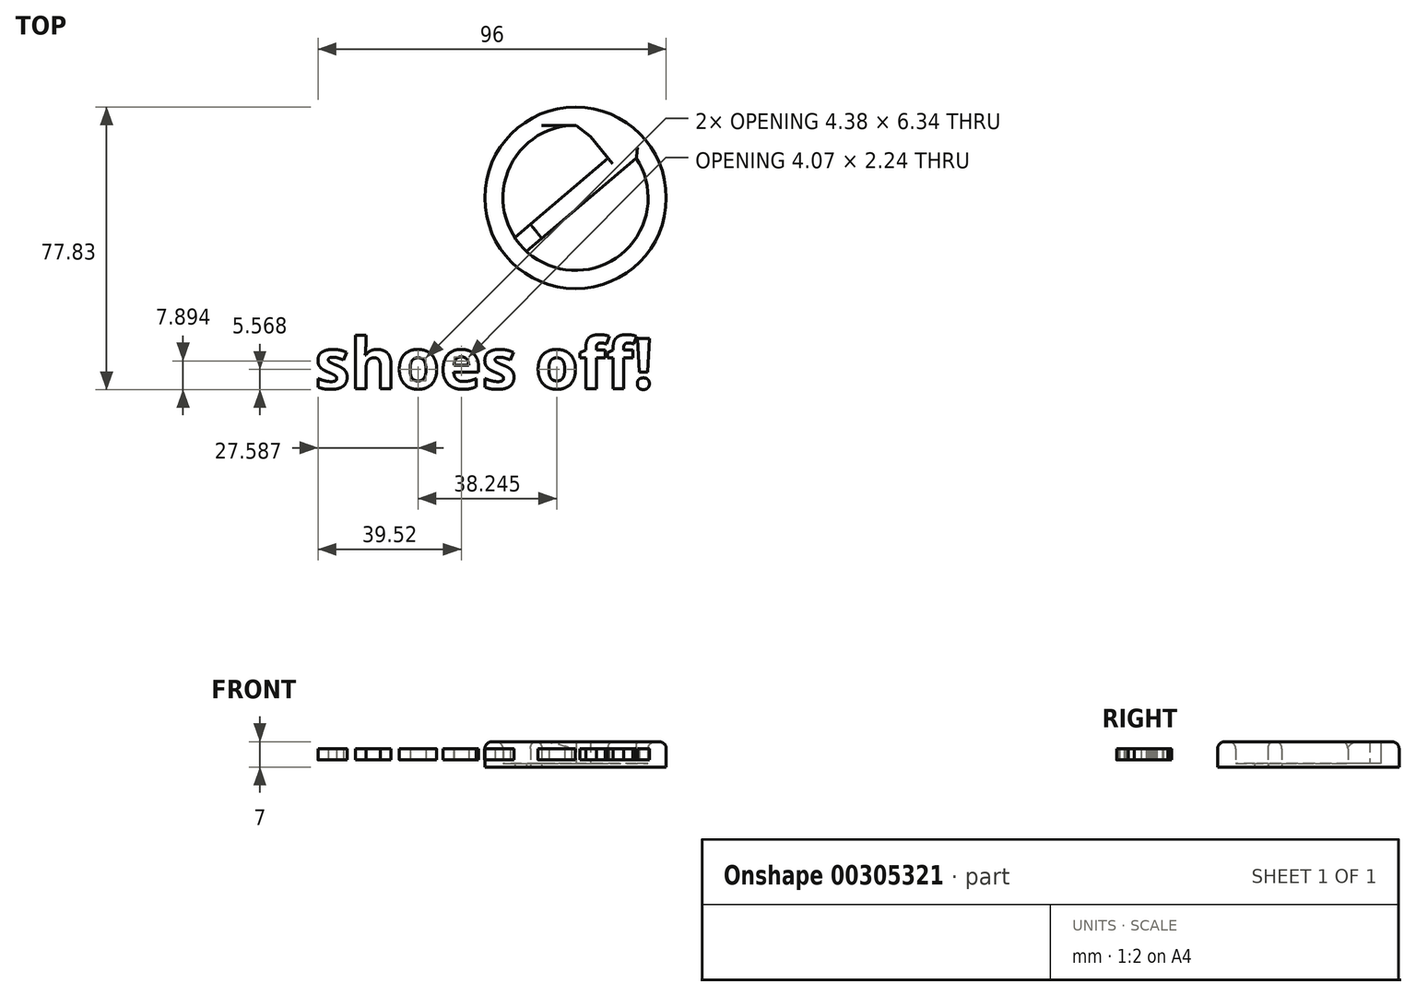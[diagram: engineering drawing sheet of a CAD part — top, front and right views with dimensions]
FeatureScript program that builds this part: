
annotation { "Feature Type Name" : "Feature", "Feature Type Description" : "" }
export const myFeature = defineFeature(function(context is Context, id is Id, definition is map)
    precondition{}
    {
        {
            var Q0;
            Q0=qCreatedBy(makeId("Top.planeOp"),FACE);
            var sketch = newSketch(context, id + "F0", { "sketchPlane" : qUnion([Q0])});
            skLineSegment(sketch, "E0.top", {"start": v(-121.35, -25.22) * mm, "end": v(78.65, -25.22) * mm});
            skLineSegment(sketch, "E0.left", {"start": v(-121.35, 24.78) * mm, "end": v(-121.35, -25.22) * mm});
            skLineSegment(sketch, "E0.right", {"start": v(78.65, 24.78) * mm, "end": v(78.65, -25.22) * mm});
            skCircle(sketch, "E1", {"center": v(37.04, 37.35) * mm, "radius": 25 * mm});
            skPoint(sketch, "E1.first.point", {"position": v(15.44, 24.78) * mm});
            skCircle(sketch, "E2", {"center": v(37.04, 37.35) * mm, "radius": 20 * mm});
            skLineSegment(sketch, "E3", {"start": v(20.32, 26.39) * mm, "end": v(50.53, 52.12) * mm});
            skLineSegment(sketch, "E4", {"start": v(53.77, 48.31) * mm, "end": v(23.56, 22.58) * mm});
            skLineSegment(sketch, "E5", {"start": v(20.32, 26.39) * mm, "end": v(23.56, 22.58) * mm, "construction": true});
            skLineSegment(sketch, "E6", {"start": v(21.94, 24.48) * mm, "end": v(52.27, 50.32) * mm, "construction": true});
            skPoint(sketch, "E7", {"position": v(58.65, 24.78) * mm});
            skLineSegment(sketch, "E8", {"start": v(-121.35, 24.78) * mm, "end": v(15.44, 24.78) * mm});
            skLineSegment(sketch, "E9", {"start": v(58.65, 24.78) * mm, "end": v(78.65, 24.78) * mm});
            skLineSegment(sketch, "E10", {"start": v(30.68, 24.1) * mm, "end": v(36.58, 27.82) * mm});
            skLineSegment(sketch, "E11", {"start": v(36.58, 27.82) * mm, "end": v(35.77, 32.31) * mm});
            skLineSegment(sketch, "E12", {"start": v(34.65, 36) * mm, "end": v(32.57, 40.8) * mm});
            skLineSegment(sketch, "E13", {"start": v(32.57, 40.8) * mm, "end": v(29.04, 43.21) * mm});
            skLineSegment(sketch, "E14", {"start": v(29.04, 43.21) * mm, "end": v(24.28, 43.73) * mm});
            skLineSegment(sketch, "E15", {"start": v(24.28, 43.73) * mm, "end": v(21.68, 41.4) * mm});
            skLineSegment(sketch, "E16", {"start": v(21.68, 41.4) * mm, "end": v(20.64, 36.9) * mm});
            skLineSegment(sketch, "E17", {"start": v(20.64, 36.9) * mm, "end": v(22.8, 32.31) * mm});
            skLineSegment(sketch, "E18", {"start": v(22.8, 32.31) * mm, "end": v(27.74, 26.17) * mm});
            skLineSegment(sketch, "E19", {"start": v(27.74, 26.17) * mm, "end": v(30.68, 24.1) * mm});
            skLineSegment(sketch, "E20", {"start": v(31.8, 22.28) * mm, "end": v(37.95, 26.17) * mm});
            skLineSegment(sketch, "E21", {"start": v(37.95, 26.17) * mm, "end": v(39.94, 24.61) * mm});
            skLineSegment(sketch, "E22", {"start": v(39.94, 24.61) * mm, "end": v(41.5, 22.02) * mm});
            skLineSegment(sketch, "E23", {"start": v(41.5, 22.02) * mm, "end": v(40.72, 18.47) * mm});
            skLineSegment(sketch, "E24", {"start": v(40.72, 18.47) * mm, "end": v(38.2, 17.09) * mm});
            skLineSegment(sketch, "E25", {"start": v(38.2, 17.09) * mm, "end": v(34.23, 17.78) * mm});
            skLineSegment(sketch, "E26", {"start": v(34.23, 17.78) * mm, "end": v(32.76, 20.03) * mm});
            skLineSegment(sketch, "E27", {"start": v(32.76, 20.03) * mm, "end": v(31.8, 22.28) * mm});
            skLineSegment(sketch, "E28", {"start": v(34.65, 36) * mm, "end": v(35.77, 32.31) * mm});
            skLineSegment(sketch, "E29", {"start": v(25.33, 53.56) * mm, "end": v(50.32, 22.39) * mm, "construction": true});
            skLineSegment(sketch, "E30.MirrorCS", {"start": v(29.21, 50.51) * mm, "end": v(29.74, 55.27) * mm});
            skLineSegment(sketch, "E31.MirrorCS", {"start": v(29.74, 55.27) * mm, "end": v(32.59, 57.3) * mm});
            skLineSegment(sketch, "E32.MirrorCS", {"start": v(32.59, 57.3) * mm, "end": v(37.2, 57.33) * mm});
            skLineSegment(sketch, "E33.MirrorCS", {"start": v(37.2, 57.33) * mm, "end": v(41.2, 54.22) * mm});
            skLineSegment(sketch, "E34.MirrorCS", {"start": v(41.2, 54.22) * mm, "end": v(46.13, 48.07) * mm});
            skLineSegment(sketch, "E35.MirrorCS", {"start": v(46.13, 48.07) * mm, "end": v(47.52, 44.75) * mm});
            skLineSegment(sketch, "E36.MirrorCS", {"start": v(47.52, 44.75) * mm, "end": v(42.6, 39.8) * mm});
            skLineSegment(sketch, "E37.MirrorCS", {"start": v(42.6, 39.8) * mm, "end": v(38.39, 41.56) * mm});
            skLineSegment(sketch, "E38.MirrorCS", {"start": v(35.03, 43.46) * mm, "end": v(38.39, 41.56) * mm});
            skLineSegment(sketch, "E39.MirrorCS", {"start": v(35.03, 43.46) * mm, "end": v(30.8, 46.54) * mm});
            skLineSegment(sketch, "E40.MirrorCS", {"start": v(30.8, 46.54) * mm, "end": v(29.21, 50.51) * mm});
            skLineSegment(sketch, "E41.MirrorCS", {"start": v(49.05, 43.26) * mm, "end": v(43.9, 38.1) * mm});
            skLineSegment(sketch, "E42.MirrorCS", {"start": v(43.9, 38.1) * mm, "end": v(45, 35.83) * mm});
            skLineSegment(sketch, "E43.MirrorCS", {"start": v(45, 35.83) * mm, "end": v(47.2, 33.74) * mm});
            skLineSegment(sketch, "E44.MirrorCS", {"start": v(47.2, 33.74) * mm, "end": v(50.82, 33.73) * mm});
            skLineSegment(sketch, "E45.MirrorCS", {"start": v(50.82, 33.73) * mm, "end": v(52.72, 35.88) * mm});
            skLineSegment(sketch, "E46.MirrorCS", {"start": v(52.72, 35.88) * mm, "end": v(52.9, 39.91) * mm});
            skLineSegment(sketch, "E47.MirrorCS", {"start": v(52.9, 39.91) * mm, "end": v(51.03, 41.84) * mm});
            skLineSegment(sketch, "E48.MirrorCS", {"start": v(51.03, 41.84) * mm, "end": v(49.05, 43.26) * mm});
            skText(sketch, "E49", { "text": "Please", "fontName": "OpenSans-Bold.ttf"});
            skText(sketch, "E50", { "text": "take your", "fontName": "OpenSans-Regular.ttf"});
            skText(sketch, "E51", { "text": "shoes off!", "fontName": "OpenSans-Bold.ttf"});
            skLineSegment(sketch, "E52.0", {"start": v(-116.35, 19.78) * mm, "end": v(19.27, 19.78) * mm});
            skLineSegment(sketch, "E52.1", {"start": v(54.82, 19.78) * mm, "end": v(73.65, 19.78) * mm});
            skLineSegment(sketch, "E52.2", {"start": v(73.65, 19.78) * mm, "end": v(73.65, -20.22) * mm});
            skLineSegment(sketch, "E52.3", {"start": v(-116.35, -20.22) * mm, "end": v(73.65, -20.22) * mm});
            skLineSegment(sketch, "E52.4", {"start": v(-116.35, 19.78) * mm, "end": v(-116.35, -20.22) * mm});
            const initialGuessF0  = {"E49": [-0.10135, 0.00366, 1, 0, 0.01112], "E50": [-0.04635, 0.00366, 1, 0, 0.008], "E51": [-0.03483, -0.01522, 1, 0, 0.014]};
            skSetInitialGuess(sketch, initialGuessF0);
            skSolve(sketch);
        }
        {
            var Q0;
            {var subQ16=sQuery(id+"F0.wireOp",EDGE,"E1");var subQ17=makeQuery(id+"F0.imprint","INTERSECT",VERTEX,{"derivedFrom":[subQ16,sQuery(id+"F0.wireOp",EDGE,"E8")]});Q0=makeQuery(id+"F0.imprint","IMPRINT",FACE,{"disambiguationData":[TD([[makeQuery(id+"F0.imprint","IMPRINT",EDGE,{"disambiguationData":[TD([[subQ17,-1.0]])],"derivedFrom":subQ16}),1.0]])]});}
            var Q1;
            {var subQ0=sQuery(id+"F0.wireOp",EDGE,"E35.MirrorCS");Q1=makeQuery(id+"F0.imprint","IMPRINT",FACE,{"disambiguationData":[TD([[makeQuery(id+"F0.imprint","IMPRINT",EDGE,{"derivedFrom":subQ0}),1.0]])]});}
            var Q2;
            {var subQ0=sQuery(id+"F0.wireOp",EDGE,"E35.MirrorCS");Q2=makeQuery(id+"F0.imprint","IMPRINT",FACE,{"disambiguationData":[TD([[makeQuery(id+"F0.imprint","IMPRINT",EDGE,{"derivedFrom":subQ0}),-1.0]])]});}
            var Q3;
            {var subQ1=sQuery(id+"F0.wireOp",EDGE,"E2");var subQ5=sQuery(id+"F0.wireOp",EDGE,"E3");var subQ6=makeQuery(id+"F0.imprint","INTERSECT",VERTEX,{"disambiguationData":[OD(0.0)],"derivedFrom":[subQ1,subQ5]});Q3=makeQuery(id+"F0.imprint","IMPRINT",FACE,{"disambiguationData":[TD([[makeQuery(id+"F0.imprint","IMPRINT",EDGE,{"disambiguationData":[TD([[subQ6,-1.0]])],"derivedFrom":subQ1}),1.0]])]});}
            var Q4;
            {var subQ1=sQuery(id+"F0.wireOp",EDGE,"E18");var subQ3=sQuery(id+"F0.wireOp",EDGE,"E3");var subQ4=makeQuery(id+"F0.imprint","INTERSECT",VERTEX,{"derivedFrom":[subQ3,subQ1]});Q4=makeQuery(id+"F0.imprint","IMPRINT",FACE,{"disambiguationData":[TD([[makeQuery(id+"F0.imprint","IMPRINT",EDGE,{"disambiguationData":[TD([[subQ4,-1.0]])],"derivedFrom":subQ3}),-1.0]])]});}
            var Q5;
            {var subQ0=sQuery(id+"F0.wireOp",EDGE,"E32.MirrorCS");var subQ1=sQuery(id+"F0.wireOp",EDGE,"E2");var subQ2=makeQuery(id+"F0.imprint","INTERSECT",VERTEX,{"derivedFrom":[subQ1,subQ0]});Q5=makeQuery(id+"F0.imprint","IMPRINT",FACE,{"disambiguationData":[TD([[makeQuery(id+"F0.imprint","IMPRINT",EDGE,{"disambiguationData":[TD([[subQ2,-1.0]])],"derivedFrom":subQ1}),-1.0]])]});}
            var Q6;
            {var subQ0=sQuery(id+"F0.wireOp",EDGE,"E25");var subQ1=sQuery(id+"F0.wireOp",EDGE,"E2");var subQ2=makeQuery(id+"F0.imprint","INTERSECT",VERTEX,{"derivedFrom":[subQ1,subQ0]});Q6=makeQuery(id+"F0.imprint","IMPRINT",FACE,{"disambiguationData":[TD([[makeQuery(id+"F0.imprint","IMPRINT",EDGE,{"disambiguationData":[TD([[subQ2,-1.0]])],"derivedFrom":subQ1}),-1.0]])]});}
            extrude(context, id + "F1", {"entities" : qUnion([Q0, Q1, Q2, Q3, Q4, Q5, Q6]), "depth" : 7 * mm});
        }
        {
            var Q0;
            {var subQ0=sQuery(id+"F0.wireOp",EDGE,"E13");Q0=makeQuery(id+"F0.imprint","IMPRINT",FACE,{"disambiguationData":[TD([[makeQuery(id+"F0.imprint","IMPRINT",EDGE,{"derivedFrom":subQ0}),1.0]])]});}
            var Q1;
            {var subQ8=sQuery(id+"F0.wireOp",EDGE,"E13");Q1=makeQuery(id+"F0.imprint","IMPRINT",FACE,{"disambiguationData":[TD([[makeQuery(id+"F0.imprint","IMPRINT",EDGE,{"derivedFrom":subQ8}),-1.0]])]});}
            var Q2;
            {var subQ1=sQuery(id+"F0.wireOp",EDGE,"E30.MirrorCS");Q2=makeQuery(id+"F0.imprint","IMPRINT",FACE,{"disambiguationData":[TD([[makeQuery(id+"F0.imprint","IMPRINT",EDGE,{"derivedFrom":subQ1}),-1.0]])]});}
            var Q3;
            {var subQ0=sQuery(id+"F0.wireOp",EDGE,"E33.MirrorCS");Q3=makeQuery(id+"F0.imprint","IMPRINT",FACE,{"disambiguationData":[TD([[makeQuery(id+"F0.imprint","IMPRINT",EDGE,{"derivedFrom":subQ0}),1.0]])]});}
            var Q4;
            {var subQ12=sQuery(id+"F0.wireOp",EDGE,"E10");Q4=makeQuery(id+"F0.imprint","IMPRINT",FACE,{"disambiguationData":[TD([[makeQuery(id+"F0.imprint","IMPRINT",EDGE,{"derivedFrom":subQ12}),-1.0]])]});}
            var Q5;
            Q5=makeQuery(id+"F0.imprint","IMPRINT",FACE,{"disambiguationData":[TD([[makeQuery(id+"F0.imprint","IMPRINT",EDGE,{"derivedFrom":sQuery(id+"F0.wireOp",EDGE,"E41.MirrorCS")}),1.0]])]});
            var Q6;
            {var subQ1=sQuery(id+"F0.wireOp",EDGE,"E10");Q6=makeQuery(id+"F0.imprint","IMPRINT",FACE,{"disambiguationData":[TD([[makeQuery(id+"F0.imprint","IMPRINT",EDGE,{"derivedFrom":subQ1}),1.0]])]});}
            var Q7;
            Q7=makeQuery(id+"F0.imprint","IMPRINT",FACE,{"disambiguationData":[TD([[makeQuery(id+"F0.imprint","IMPRINT",EDGE,{"derivedFrom":sQuery(id+"F0.wireOp",EDGE,"E20")}),-1.0]])]});
            extrude(context, id + "F2", {"entities" : qUnion([Q0, Q1, Q2, Q3, Q4, Q5, Q6, Q7]), "operationType" : NewBodyOperationType.ADD, "depth" : 1 * mm});
        }
        {
            var Q0;
            Q0=makeQuery(id+"F0.imprint","IMPRINT",FACE,{"disambiguationData":[TD([[makeQuery(id+"F0.imprint","IMPRINT",EDGE,{"derivedFrom":sQuery(id+"F0.wireOp",EDGE,"E51.sketch_text.stroke-0")}),-1.0]])]});
            var Q1;
            Q1=makeQuery(id+"F0.imprint","IMPRINT",FACE,{"disambiguationData":[TD([[makeQuery(id+"F0.imprint","IMPRINT",EDGE,{"derivedFrom":sQuery(id+"F0.wireOp",EDGE,"E51.sketch_text.stroke-26")}),-1.0]])]});
            var Q2;
            Q2=makeQuery(id+"F0.imprint","IMPRINT",FACE,{"disambiguationData":[TD([[makeQuery(id+"F0.imprint","IMPRINT",EDGE,{"derivedFrom":sQuery(id+"F0.wireOp",EDGE,"E51.sketch_text.stroke-43")}),-1.0]])]});
            var Q3;
            Q3=makeQuery(id+"F0.imprint","IMPRINT",FACE,{"disambiguationData":[TD([[makeQuery(id+"F0.imprint","IMPRINT",EDGE,{"derivedFrom":sQuery(id+"F0.wireOp",EDGE,"E51.sketch_text.stroke-61")}),-1.0]])]});
            var Q4;
            Q4=makeQuery(id+"F0.imprint","IMPRINT",FACE,{"disambiguationData":[TD([[makeQuery(id+"F0.imprint","IMPRINT",EDGE,{"derivedFrom":sQuery(id+"F0.wireOp",EDGE,"E51.sketch_text.stroke-81")}),-1.0]])]});
            var Q5;
            Q5=makeQuery(id+"F0.imprint","IMPRINT",FACE,{"disambiguationData":[TD([[makeQuery(id+"F0.imprint","IMPRINT",EDGE,{"derivedFrom":sQuery(id+"F0.wireOp",EDGE,"E51.sketch_text.stroke-107")}),-1.0]])]});
            var Q6;
            Q6=makeQuery(id+"F0.imprint","IMPRINT",FACE,{"disambiguationData":[TD([[makeQuery(id+"F0.imprint","IMPRINT",EDGE,{"derivedFrom":sQuery(id+"F0.wireOp",EDGE,"E51.sketch_text.stroke-125")}),-1.0]])]});
            var Q7;
            Q7=makeQuery(id+"F0.imprint","IMPRINT",FACE,{"disambiguationData":[TD([[makeQuery(id+"F0.imprint","IMPRINT",EDGE,{"derivedFrom":sQuery(id+"F0.wireOp",EDGE,"E51.sketch_text.stroke-143")}),-1.0]])]});
            var Q8;
            Q8=makeQuery(id+"F0.imprint","IMPRINT",FACE,{"disambiguationData":[TD([[makeQuery(id+"F0.imprint","IMPRINT",EDGE,{"derivedFrom":sQuery(id+"F0.wireOp",EDGE,"E51.sketch_text.stroke-161")}),-1.0]])]});
            var Q9;
            Q9=makeQuery(id+"F0.imprint","IMPRINT",FACE,{"disambiguationData":[TD([[makeQuery(id+"F0.imprint","IMPRINT",EDGE,{"derivedFrom":sQuery(id+"F0.wireOp",EDGE,"E51.sketch_text.stroke-165")}),-1.0]])]});
            extrude(context, id + "F3", {"entities" : qUnion([Q0, Q1, Q2, Q3, Q4, Q5, Q6, Q7, Q8, Q9]), "depth" : 5 * mm, "hasSecondDirection" : true, "secondDirectionOppositeDirection" : false, "secondDirectionDepth" : 2 * mm});
        }
        {
            var Q0;
            Q0=makeQuery(id+"F1.opExtrude","CAP_EDGE",EDGE,{"disambiguationData":[OSD([sQuery(id+"F0.wireOp",EDGE,"E1")])],"isStart":false});
            var Q1;
            {var subQ0=sQuery(id+"F0.wireOp",EDGE,"E3");var subQ1=sQuery(id+"F0.wireOp",EDGE,"E2");var subQ3=makeQuery(id+"F0.imprint","INTERSECT",VERTEX,{"derivedFrom":[subQ1,sQuery(id+"F0.wireOp",EDGE,"E32.MirrorCS")]});Q1=makeQuery(id+"F1.opExtrude","CAP_EDGE",EDGE,{"disambiguationData":[OSD([subQ1]),TDD([makeQuery(id+"F0.imprint","IMPRINT",EDGE,{"disambiguationData":[TD([[makeQuery(id+"F0.imprint","INTERSECT",VERTEX,{"disambiguationData":[OD(1.0)],"derivedFrom":[subQ1,subQ0]}),-1.0]])],"derivedFrom":subQ1}),makeQuery(id+"F0.imprint","IMPRINT",EDGE,{"disambiguationData":[TD([[subQ3,-1.0]])],"derivedFrom":subQ1}),makeQuery(id+"F0.imprint","IMPRINT",EDGE,{"disambiguationData":[TD([[makeQuery(id+"F0.imprint","INTERSECT",VERTEX,{"disambiguationData":[OD(0.0)],"derivedFrom":[subQ1,subQ0]}),1.0]])],"derivedFrom":subQ1})])],"isStart":false});}
            var Q2;
            {var subQ0=sQuery(id+"F0.wireOp",EDGE,"E4");var subQ1=sQuery(id+"F0.wireOp",EDGE,"E2");var subQ3=makeQuery(id+"F0.imprint","INTERSECT",VERTEX,{"derivedFrom":[subQ1,sQuery(id+"F0.wireOp",EDGE,"E25")]});Q2=makeQuery(id+"F1.opExtrude","CAP_EDGE",EDGE,{"disambiguationData":[OSD([subQ1]),TDD([makeQuery(id+"F0.imprint","IMPRINT",EDGE,{"disambiguationData":[TD([[makeQuery(id+"F0.imprint","INTERSECT",VERTEX,{"disambiguationData":[OD(1.0)],"derivedFrom":[subQ1,subQ0]}),-1.0]])],"derivedFrom":subQ1}),makeQuery(id+"F0.imprint","IMPRINT",EDGE,{"disambiguationData":[TD([[subQ3,-1.0]])],"derivedFrom":subQ1}),makeQuery(id+"F0.imprint","IMPRINT",EDGE,{"disambiguationData":[TD([[makeQuery(id+"F0.imprint","INTERSECT",VERTEX,{"disambiguationData":[OD(0.0)],"derivedFrom":[subQ1,subQ0]}),1.0]])],"derivedFrom":subQ1})])],"isStart":false});}
            var Q3;
            Q3=makeQuery(id+"F1.opExtrude","CAP_EDGE",EDGE,{"disambiguationData":[OSD([sQuery(id+"F0.wireOp",EDGE,"E4")])],"isStart":false});
            var Q4;
            Q4=makeQuery(id+"F1.opExtrude","CAP_EDGE",EDGE,{"disambiguationData":[OSD([sQuery(id+"F0.wireOp",EDGE,"E3")])],"isStart":false});
            fillet(context, id + "F4", {"entities" : qUnion([Q0, Q1, Q2, Q3, Q4]), "radius" : 2 * mm, "tangentPropagation" : true, "allowEdgeOverflow" : false});
        }
    });
